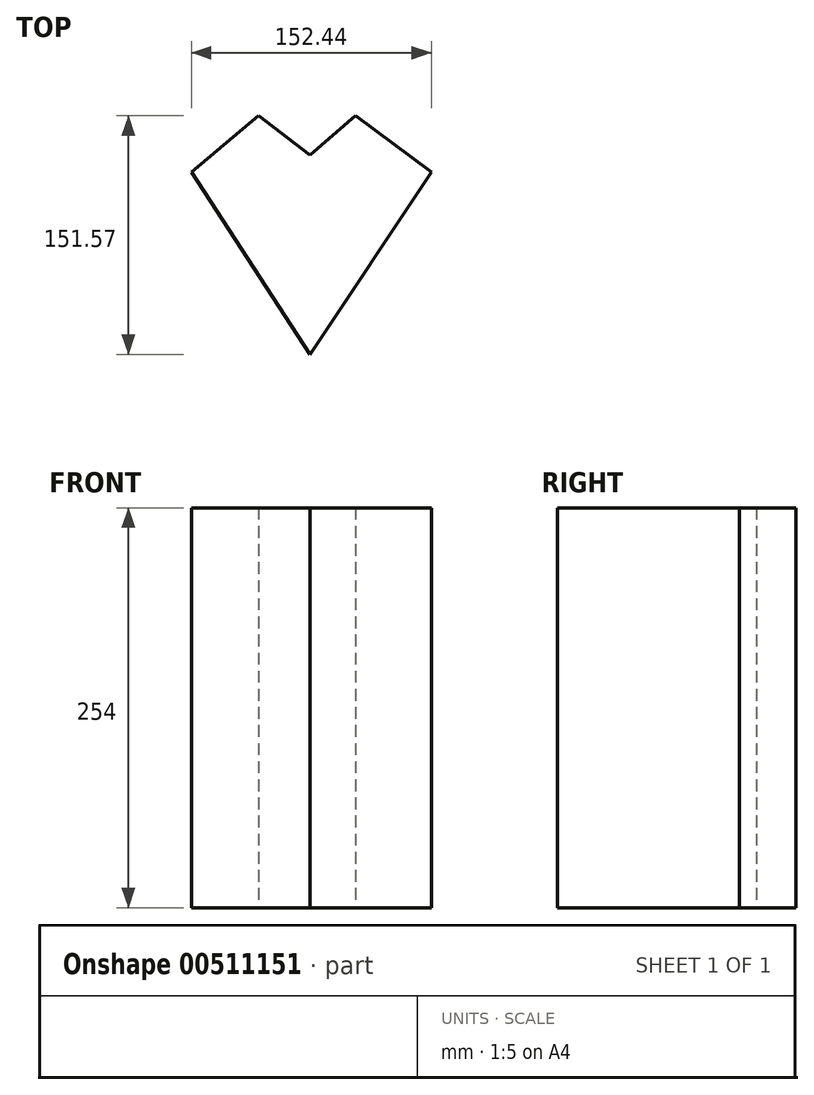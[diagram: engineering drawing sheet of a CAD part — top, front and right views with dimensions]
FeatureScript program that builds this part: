
annotation { "Feature Type Name" : "Feature", "Feature Type Description" : "" }
export const myFeature = defineFeature(function(context is Context, id is Id, definition is map)
    precondition{}
    {
        {
            var Q0;
            Q0=qCreatedBy(makeId("Top.planeOp"),FACE);
            var sketch = newSketch(context, id + "F0", { "sketchPlane" : qUnion([Q0])});
            skLineSegment(sketch, "E0", {"start": v(0, 50.57) * mm, "end": v(-32.65, 75.64) * mm});
            skLineSegment(sketch, "E1", {"start": v(-32.65, 75.64) * mm, "end": v(-75.2, 39.79) * mm});
            skLineSegment(sketch, "E2", {"start": v(-75.2, 39.79) * mm, "end": v(0, -75.93) * mm});
            skLineSegment(sketch, "E3", {"start": v(0, -75.93) * mm, "end": v(77.24, 39.79) * mm});
            skLineSegment(sketch, "E4", {"start": v(77.24, 39.79) * mm, "end": v(29.15, 75.64) * mm});
            skLineSegment(sketch, "E5", {"start": v(29.15, 75.64) * mm, "end": v(0, 50.57) * mm});
            skSolve(sketch);
        }
        {
            var Q0;
            Q0=makeQuery(id+"F0.imprint","IMPRINT",FACE,{"disambiguationData":[TD([[makeQuery(id+"F0.imprint","IMPRINT",EDGE,{"derivedFrom":sQuery(id+"F0.wireOp",EDGE,"E0")}),1.0]])]});
            extrude(context, id + "F1", {"entities" : qUnion([Q0]), "endBound" : BoundingType.SYMMETRIC, "depth" : 254 * mm});
        }
    });
